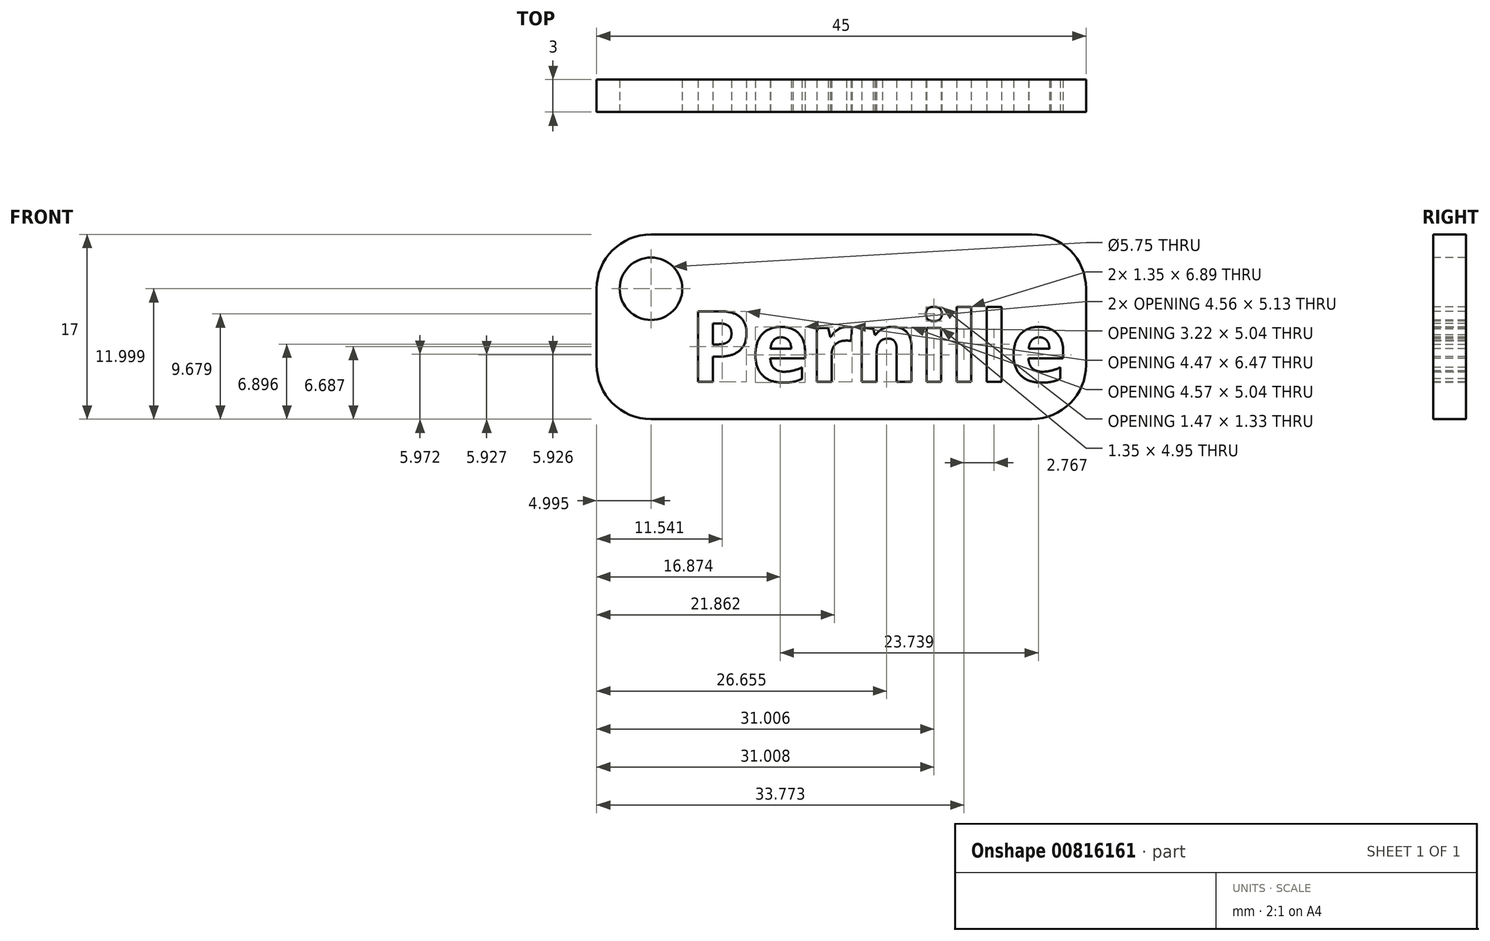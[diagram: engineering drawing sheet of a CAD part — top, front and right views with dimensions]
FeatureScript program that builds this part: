
annotation { "Feature Type Name" : "Feature", "Feature Type Description" : "" }
export const myFeature = defineFeature(function(context is Context, id is Id, definition is map)
    precondition{}
    {
        {
            var Q0;
            Q0=qCreatedBy(makeId("Front.planeOp"),FACE);
            var sketch = newSketch(context, id + "F0", { "sketchPlane" : qUnion([Q0])});
            skLineSegment(sketch, "E0.bottom", {"start": v(-7.88, 2.63) * mm, "end": v(27.12, 2.63) * mm});
            skLineSegment(sketch, "E0.top", {"start": v(-7.88, -14.37) * mm, "end": v(27.12, -14.37) * mm});
            skLineSegment(sketch, "E0.left", {"start": v(-12.88, -2.37) * mm, "end": v(-12.88, -9.37) * mm});
            skLineSegment(sketch, "E0.right", {"start": v(32.12, -2.37) * mm, "end": v(32.12, -9.37) * mm});
            skPoint(sketch, "E1.visualSharp", {"position": v(-12.88, 2.63) * mm});
            skArc(sketch, "E1.filletArc", {"start": v(-7.88, 2.63) * mm, "mid": v(-11.42, 1.16) * mm, "end": v(-12.88, -2.37) * mm});
            skPoint(sketch, "E2.visualSharp", {"position": v(32.12, 2.63) * mm});
            skArc(sketch, "E2.filletArc", {"start": v(32.12, -2.37) * mm, "mid": v(30.65, 1.16) * mm, "end": v(27.12, 2.63) * mm});
            skPoint(sketch, "E3.visualSharp", {"position": v(32.12, -14.37) * mm});
            skArc(sketch, "E3.filletArc", {"start": v(27.12, -14.37) * mm, "mid": v(30.65, -12.9) * mm, "end": v(32.12, -9.37) * mm});
            skPoint(sketch, "E4.visualSharp", {"position": v(-12.88, -14.37) * mm});
            skArc(sketch, "E4.filletArc", {"start": v(-12.88, -9.37) * mm, "mid": v(-11.42, -12.9) * mm, "end": v(-7.88, -14.37) * mm});
            skSolve(sketch);
        }
        {
            var Q0;
            Q0=makeQuery(id+"F0.imprint","IMPRINT",FACE,{"disambiguationData":[TD([[makeQuery(id+"F0.imprint","IMPRINT",EDGE,{"derivedFrom":sQuery(id+"F0.wireOp",EDGE,"E0.bottom")}),-1.0]])]});
            extrude(context, id + "F1", {"entities" : qUnion([Q0]), "depth" : 3 * mm, "offsetDistance" : 25 * mm});
        }
        {
            var Q0;
            Q0=makeQuery(id+"F1.opExtrude","CAP_FACE",FACE,{"disambiguationData":[OSD([sQuery(id+"F0.wireOp",EDGE,"E0.bottom"),sQuery(id+"F0.wireOp",EDGE,"E0.top"),sQuery(id+"F0.wireOp",EDGE,"E0.left"),sQuery(id+"F0.wireOp",EDGE,"E0.right"),sQuery(id+"F0.wireOp",EDGE,"E1.filletArc"),sQuery(id+"F0.wireOp",EDGE,"E2.filletArc"),sQuery(id+"F0.wireOp",EDGE,"E3.filletArc"),sQuery(id+"F0.wireOp",EDGE,"E4.filletArc")])],"isStart":false});
            var sketch = newSketch(context, id + "F2", { "sketchPlane" : qUnion([Q0])});
            skCircle(sketch, "E5", {"center": v(-7.88, -2.37) * mm, "radius": 2.88 * mm});
            skSolve(sketch);
        }
        {
            var Q0;
            Q0 = qSketchRegion(id + "F2", true);
            extrude(context, id + "F3", {"entities" : qUnion([Q0]), "operationType" : NewBodyOperationType.REMOVE, "oppositeDirection" : true, "depth" : 3 * mm, "offsetDistance" : 25 * mm});
        }
        {
            var Q0;
            Q0=makeQuery(id+"F1.opExtrude","CAP_FACE",FACE,{"disambiguationData":[OSD([sQuery(id+"F0.wireOp",EDGE,"E0.bottom"),sQuery(id+"F0.wireOp",EDGE,"E0.top"),sQuery(id+"F0.wireOp",EDGE,"E0.left"),sQuery(id+"F0.wireOp",EDGE,"E0.right"),sQuery(id+"F0.wireOp",EDGE,"E1.filletArc"),sQuery(id+"F0.wireOp",EDGE,"E2.filletArc"),sQuery(id+"F0.wireOp",EDGE,"E3.filletArc"),sQuery(id+"F0.wireOp",EDGE,"E4.filletArc")])],"isStart":false});
            var sketch = newSketch(context, id + "F4", { "sketchPlane" : qUnion([Q0])});
            skText(sketch, "E6", { "text": "Pernille", "fontName": "OpenSans-Bold.ttf"});
            const initialGuessF4  = {"E6": [-0.00439, -0.01092, 1, 0, 0.00653]};
            skSetInitialGuess(sketch, initialGuessF4);
            skSolve(sketch);
        }
        {
            var Q0;
            Q0 = qSketchRegion(id + "F4", true);
            extrude(context, id + "F5", {"entities" : qUnion([Q0]), "operationType" : NewBodyOperationType.REMOVE, "oppositeDirection" : true, "depth" : 3 * mm, "offsetDistance" : 25 * mm});
        }
    });
